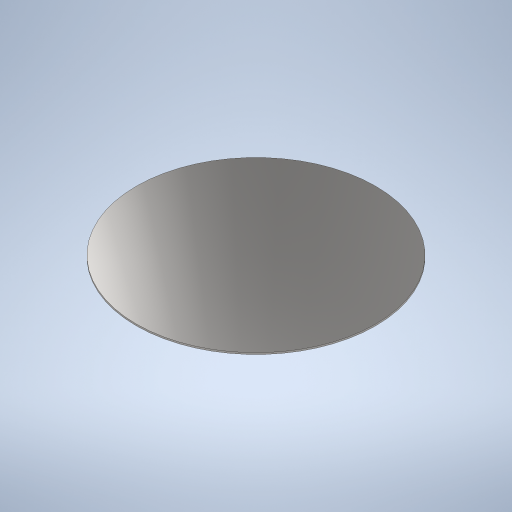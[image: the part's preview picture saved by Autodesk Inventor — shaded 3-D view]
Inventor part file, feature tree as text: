
AUTODESK INVENTOR PART (.ipt)
format: ipt  version: 2024.2 (Build 282272000, 272)  size: 240,640 bytes
history: native  units: mm
features: extrude x1, sketch x1
ambient origin geometry x8: Origin, YZ Plane, XZ Plane, XY Plane, X Axis, Y Axis, Z Axis, Center Point
bodies: Solid1 (feature_tree)
feature tree (2):
  extrude  "Extrusion1"  Depth=3.0mm TaperAngle=0.0deg
  sketch  "Sketch1"  dims[d0=450.0mm d1=3.0mm d2=0.0mm]
